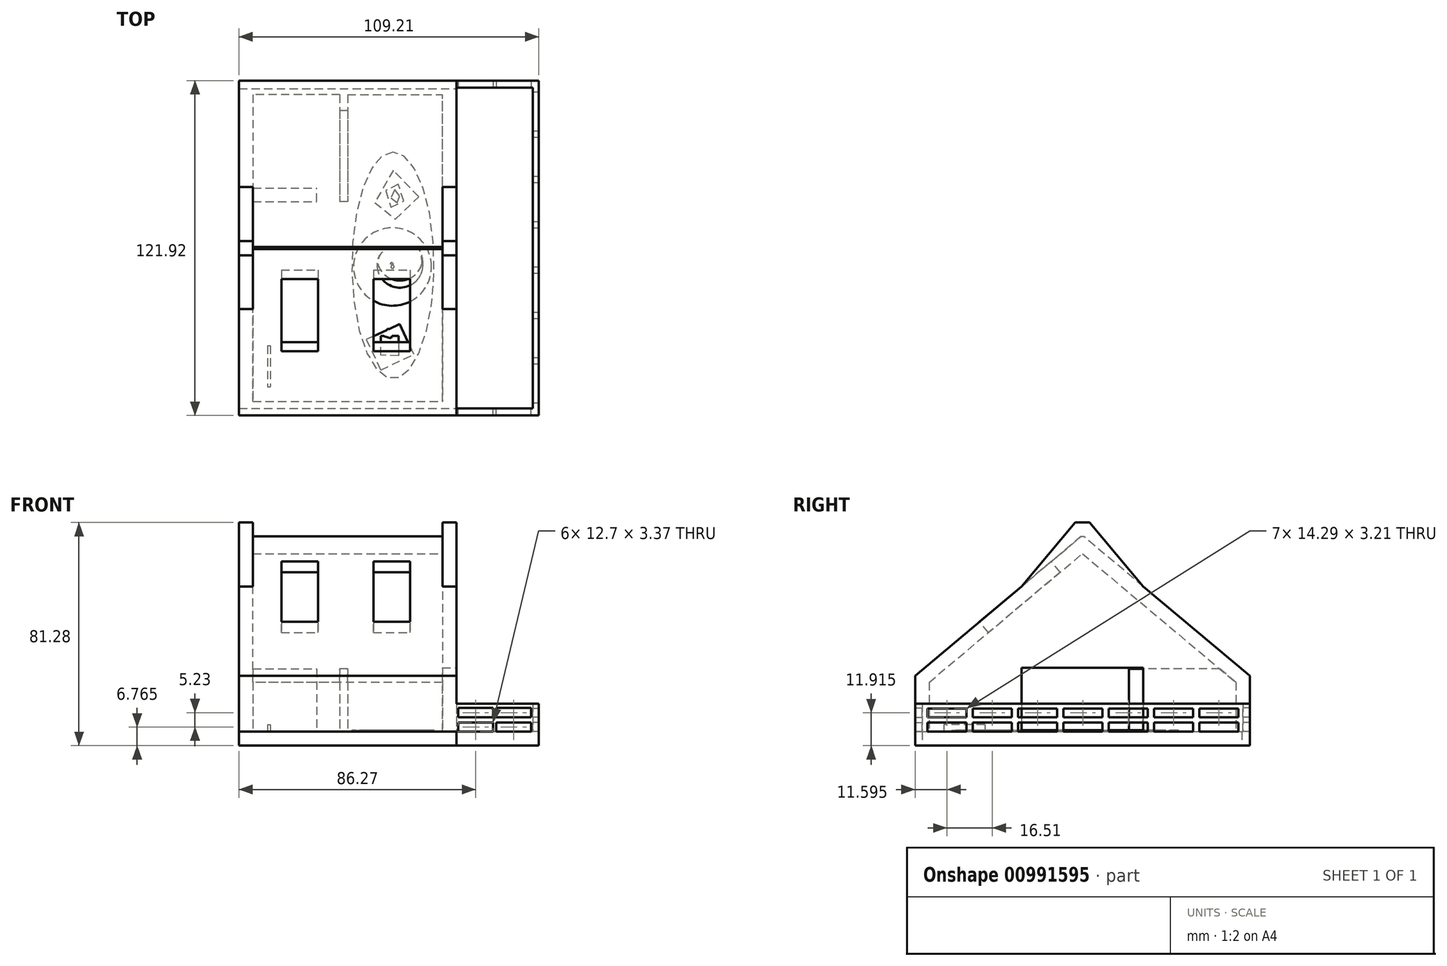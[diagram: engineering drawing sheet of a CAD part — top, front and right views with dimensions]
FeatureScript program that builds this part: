
annotation { "Feature Type Name" : "Feature", "Feature Type Description" : "" }
export const myFeature = defineFeature(function(context is Context, id is Id, definition is map)
    precondition{}
    {
        {
            var Q0;
            Q0=qCreatedBy(makeId("Top.planeOp"),FACE);
            var sketch = newSketch(context, id + "F0", { "sketchPlane" : qUnion([Q0])});
            skLineSegment(sketch, "E0.bottom", {"start": v(-69.71, 93.3) * mm, "end": v(39.5, 93.3) * mm});
            skLineSegment(sketch, "E0.top", {"start": v(-69.71, -28.62) * mm, "end": v(39.5, -28.62) * mm});
            skLineSegment(sketch, "E0.left", {"start": v(-69.71, 93.3) * mm, "end": v(-69.71, -28.62) * mm});
            skLineSegment(sketch, "E0.right", {"start": v(39.5, 93.3) * mm, "end": v(39.5, -28.62) * mm});
            skSolve(sketch);
        }
        {
            var Q0;
            Q0=makeQuery(id+"F0.imprint","IMPRINT",FACE,{"disambiguationData":[TD([[makeQuery(id+"F0.imprint","IMPRINT",EDGE,{"derivedFrom":sQuery(id+"F0.wireOp",EDGE,"E0.bottom")}),-1.0]])]});
            extrude(context, id + "F1", {"entities" : qUnion([Q0]), "depth" : 76.2 * mm, "offsetDistance" : 25.4 * mm});
        }
        {
            var Q0;
            Q0=makeQuery(id+"F1.opExtrude","CAP_FACE",FACE,{"disambiguationData":[OSD([sQuery(id+"F0.wireOp",EDGE,"E0.bottom"),sQuery(id+"F0.wireOp",EDGE,"E0.top"),sQuery(id+"F0.wireOp",EDGE,"E0.left"),sQuery(id+"F0.wireOp",EDGE,"E0.right")])],"isStart":false});
            var sketch = newSketch(context, id + "F2", { "sketchPlane" : qUnion([Q0])});
            skLineSegment(sketch, "E1.right", {"start": v(9.5, -28.62) * mm, "end": v(9.5, 93.3) * mm});
            skLineSegment(sketch, "E2.bottom", {"start": v(9.5, -28.62) * mm, "end": v(39.5, -28.62) * mm});
            skLineSegment(sketch, "E2.top", {"start": v(9.5, 93.3) * mm, "end": v(39.5, 93.3) * mm});
            skLineSegment(sketch, "E2.right", {"start": v(39.5, -28.62) * mm, "end": v(39.5, 93.3) * mm});
            skSolve(sketch);
        }
        {
            var Q0;
            Q0 = qSketchRegion(id + "F2", true);
            extrude(context, id + "F3", {"entities" : qUnion([Q0]), "operationType" : NewBodyOperationType.REMOVE, "oppositeDirection" : true, "depth" : 71.12 * mm, "offsetDistance" : 25.4 * mm});
        }
        {
            var Q0;
            Q0=makeQuery(id+"F1.opExtrude","CAP_EDGE",EDGE,{"disambiguationData":[OSD([sQuery(id+"F0.wireOp",EDGE,"E0.bottom")])],"isStart":false});
            var Q1;
            Q1=makeQuery(id+"F1.opExtrude","CAP_EDGE",EDGE,{"disambiguationData":[OSD([sQuery(id+"F0.wireOp",EDGE,"E0.top")])],"isStart":false});
            chamfer(context, id + "F4", {"entities" : qUnion([Q0, Q1]), "chamferType" : ChamferType.OFFSET_ANGLE, "width" : 50.8 * mm, "oppositeDirection" : false, "angle" : 50 * degree, "tangentPropagation" : true});
        }
        {
            var Q0;
            Q0=makeQuery(id+"F3.boolean.opBoolean","COPY",FACE,{"derivedFrom":makeQuery(id+"F3.opExtrude","SWEPT_FACE",FACE,{"disambiguationData":[OSD([sQuery(id+"F2.wireOp",EDGE,"E1.right")])]})});
            var Q1;
            Q1=makeQuery(id+"F1.opExtrude","SWEPT_FACE",FACE,{"disambiguationData":[OSD([sQuery(id+"F0.wireOp",EDGE,"E0.left")])]});
            shell(context, id + "F5", {"entities" : qUnion([Q0, Q1]), "thickness" : 5.08 * mm});
        }
        {
            var Q0;
            Q0=makeQuery(id+"F5.opShell","OFFSET_FACE",FACE,{"disambiguationData":[OSD([sQuery(id+"F0.wireOp",EDGE,"E0.bottom"),sQuery(id+"F0.wireOp",EDGE,"E0.top"),sQuery(id+"F0.wireOp",EDGE,"E0.left"),sQuery(id+"F0.wireOp",EDGE,"E0.right"),sQuery(id+"F2.wireOp",EDGE,"E2.bottom"),sQuery(id+"F2.wireOp",EDGE,"E2.top"),sQuery(id+"F2.wireOp",EDGE,"E1.right"),sQuery(id+"F2.wireOp",EDGE,"E2.right")])]});
            var sketch = newSketch(context, id + "F6", { "sketchPlane" : qUnion([Q0])});
            skPoint(sketch, "E3.oppositeSnap0", {"position": v(9.5, -26.08) * mm});
            skLineSegment(sketch, "E3.bottom", {"start": v(9.5, -28.62) * mm, "end": v(39.5, -28.62) * mm});
            skLineSegment(sketch, "E3.top", {"start": v(9.5, -26.08) * mm, "end": v(39.5, -26.08) * mm});
            skLineSegment(sketch, "E3.left", {"start": v(9.5, -28.62) * mm, "end": v(9.5, -26.08) * mm});
            skLineSegment(sketch, "E3.right", {"start": v(39.5, -28.62) * mm, "end": v(39.5, -26.08) * mm});
            skPoint(sketch, "E4.oppositeSnap0", {"position": v(9.5, 90.76) * mm});
            skLineSegment(sketch, "E4.bottom", {"start": v(9.5, 93.3) * mm, "end": v(39.5, 93.3) * mm});
            skLineSegment(sketch, "E4.top", {"start": v(9.5, 90.76) * mm, "end": v(39.5, 90.76) * mm});
            skLineSegment(sketch, "E4.left", {"start": v(9.5, 93.3) * mm, "end": v(9.5, 90.76) * mm});
            skLineSegment(sketch, "E4.right", {"start": v(39.5, 93.3) * mm, "end": v(39.5, 90.76) * mm});
            skLineSegment(sketch, "E5.bottom", {"start": v(39.5, -28.62) * mm, "end": v(37.37, -28.62) * mm});
            skLineSegment(sketch, "E5.top", {"start": v(39.5, 93.3) * mm, "end": v(37.37, 93.3) * mm});
            skLineSegment(sketch, "E5.left", {"start": v(39.5, -28.62) * mm, "end": v(39.5, 93.3) * mm});
            skLineSegment(sketch, "E5.right", {"start": v(37.37, -28.62) * mm, "end": v(37.37, 93.3) * mm});
            skLineSegment(sketch, "E6.bottom", {"start": v(9.5, -23.54) * mm, "end": v(4.43, -23.54) * mm});
            skLineSegment(sketch, "E6.top", {"start": v(9.5, 88.22) * mm, "end": v(4.43, 88.22) * mm});
            skLineSegment(sketch, "E6.left", {"start": v(9.5, -23.54) * mm, "end": v(9.5, 88.22) * mm});
            skLineSegment(sketch, "E6.right", {"start": v(4.43, -23.54) * mm, "end": v(4.43, 88.22) * mm});
            skLineSegment(sketch, "E7.bottom", {"start": v(-69.71, 88.22) * mm, "end": v(-64.63, 88.22) * mm});
            skLineSegment(sketch, "E7.top", {"start": v(-69.71, -23.54) * mm, "end": v(-64.63, -23.54) * mm});
            skLineSegment(sketch, "E7.left", {"start": v(-69.71, 88.22) * mm, "end": v(-69.71, -23.54) * mm});
            skLineSegment(sketch, "E7.right", {"start": v(-64.63, 88.22) * mm, "end": v(-64.63, -23.54) * mm});
            skLineSegment(sketch, "E8.bottom", {"start": v(-30.1, 88.22) * mm, "end": v(-32.97, 88.22) * mm});
            skLineSegment(sketch, "E8.top", {"start": v(-30.1, 49.23) * mm, "end": v(-32.97, 49.23) * mm});
            skLineSegment(sketch, "E8.left", {"start": v(-30.1, 88.22) * mm, "end": v(-30.1, 49.23) * mm});
            skLineSegment(sketch, "E8.right", {"start": v(-32.97, 88.22) * mm, "end": v(-32.97, 49.23) * mm});
            skLineSegment(sketch, "E9.bottom", {"start": v(-64.63, 49.23) * mm, "end": v(-41.45, 49.23) * mm});
            skLineSegment(sketch, "E9.top", {"start": v(-64.63, 54.2) * mm, "end": v(-41.45, 54.2) * mm});
            skLineSegment(sketch, "E9.left", {"start": v(-64.63, 49.23) * mm, "end": v(-64.63, 54.2) * mm});
            skLineSegment(sketch, "E9.right", {"start": v(-41.45, 49.23) * mm, "end": v(-41.45, 54.2) * mm});
            skEllipse(sketch, "E10", {"center": v(-13.6, 26.06) * mm, "majorRadius": 41.26 * mm, "minorRadius": 14.98 * mm, "majorAxis": v(0, 1)});
            skSolve(sketch);
        }
        {
            var Q0;
            Q0=makeQuery(id+"F6.imprint","IMPRINT",FACE,{"disambiguationData":[TD([[makeQuery(id+"F6.imprint","IMPRINT",EDGE,{"derivedFrom":sQuery(id+"F6.wireOp",EDGE,"E7.bottom")}),-1.0]])]});
            var Q1;
            Q1=makeQuery(id+"F6.imprint","IMPRINT",FACE,{"disambiguationData":[TD([[makeQuery(id+"F6.imprint","IMPRINT",EDGE,{"derivedFrom":sQuery(id+"F6.wireOp",EDGE,"E6.bottom")}),1.0]])]});
            var Q2;
            Q2 = qSketchRegion(id + "F9", true);
            extrude(context, id + "F7", {"entities" : qUnion([Q0, Q1, Q2]), "operationType" : NewBodyOperationType.ADD, "depth" : 76.2 * mm, "offsetDistance" : 25.4 * mm});
        }
        {
            var Q0;
            Q0=makeQuery(id+"F7.opExtrude","CAP_EDGE",EDGE,{"disambiguationData":[OSD([sQuery(id+"F6.wireOp",EDGE,"E6.top")])],"isStart":false});
            var Q1;
            Q1=makeQuery(id+"F7.opExtrude","CAP_EDGE",EDGE,{"disambiguationData":[OSD([sQuery(id+"F6.wireOp",EDGE,"E7.bottom")])],"isStart":false});
            var Q2;
            Q2=makeQuery(id+"F7.opExtrude","CAP_EDGE",EDGE,{"disambiguationData":[OSD([sQuery(id+"F6.wireOp",EDGE,"E6.bottom")])],"isStart":false});
            chamfer(context, id + "F8", {"entities" : qUnion([Q0, Q1, Q2]), "chamferType" : ChamferType.OFFSET_ANGLE, "width" : 63.5 * mm, "oppositeDirection" : false, "angle" : 40 * degree});
        }
        {
            var Q0;
            Q0=makeQuery(id+"F7.boolean.opBoolean","MERGE",FACE,{"derivedFrom":[makeQuery(id+"F1.opExtrude","SWEPT_FACE",FACE,{"disambiguationData":[OSD([sQuery(id+"F0.wireOp",EDGE,"E0.left")])]}),makeQuery(id+"F7.opExtrude","SWEPT_FACE",FACE,{"disambiguationData":[OSD([sQuery(id+"F6.wireOp",EDGE,"E7.left")])]})]});
            var sketch = newSketch(context, id + "F9", { "sketchPlane" : qUnion([Q0])});
            skLineSegment(sketch, "E11.0.0", {"start": v(-31.92, 76.2) * mm, "end": v(23.54, 29.66) * mm});
            skLineSegment(sketch, "E11.0.2", {"start": v(23.54, 29.66) * mm, "end": v(28.62, 25.4) * mm});
            skLineSegment(sketch, "E11.0.4", {"start": v(28.62, 25.4) * mm, "end": v(-10.15, 57.94) * mm});
            skLineSegment(sketch, "E11.0.6", {"start": v(-10.15, 57.94) * mm, "end": v(-31.92, 76.2) * mm});
            skLineSegment(sketch, "E12.0.0", {"start": v(-31.92, 76.2) * mm, "end": v(-10.15, 57.94) * mm});
            skLineSegment(sketch, "E12.0.1", {"start": v(-10.15, 57.94) * mm, "end": v(-29.74, 81.28) * mm});
            skLineSegment(sketch, "E12.0.2", {"start": v(-29.74, 81.28) * mm, "end": v(-34.94, 81.28) * mm});
            skLineSegment(sketch, "E12.0.3", {"start": v(-34.94, 81.28) * mm, "end": v(-54.52, 57.94) * mm});
            skLineSegment(sketch, "E12.0.4", {"start": v(-54.52, 57.94) * mm, "end": v(-32.76, 76.2) * mm});
            skLineSegment(sketch, "E12.0.5", {"start": v(-32.76, 76.2) * mm, "end": v(-31.92, 76.2) * mm});
            skLineSegment(sketch, "E13.0.1", {"start": v(-54.52, 57.94) * mm, "end": v(-93.3, 25.4) * mm});
            skLineSegment(sketch, "E13.0.2", {"start": v(-93.3, 25.4) * mm, "end": v(-93.3, 0) * mm});
            skLineSegment(sketch, "E13.0.3", {"start": v(-93.3, 0) * mm, "end": v(28.62, 0) * mm});
            skLineSegment(sketch, "E13.0.4", {"start": v(28.62, 0) * mm, "end": v(28.62, 25.4) * mm});
            skLineSegment(sketch, "E13.0.5", {"start": v(28.62, 25.4) * mm, "end": v(23.54, 29.66) * mm});
            skLineSegment(sketch, "E13.0.6", {"start": v(23.54, 29.66) * mm, "end": v(23.54, 81.28) * mm});
            skLineSegment(sketch, "E13.0.7", {"start": v(23.54, 81.28) * mm, "end": v(-34.94, 81.28) * mm});
            skSolve(sketch);
        }
        {
            var Q0;
            Q0=makeQuery(id+"F9.imprint","IMPRINT",FACE,{"disambiguationData":[TD([[makeQuery(id+"F9.imprint","IMPRINT",EDGE,{"derivedFrom":sQuery(id+"F9.wireOp",EDGE,"E11.0.4")}),-1.0]])]});
            extrude(context, id + "F10", {"entities" : qUnion([Q0]), "operationType" : NewBodyOperationType.REMOVE, "oppositeDirection" : true, "depth" : 25.4 * mm, "offsetDistance" : 25.4 * mm});
        }
        {
            var Q0;
            {var subQ0=sQuery(id+"F6.wireOp",EDGE,"E3.bottom");Q0=makeQuery(id+"F6.imprint","IMPRINT",FACE,{"disambiguationData":[TD([[makeQuery(id+"F6.imprint","IMPRINT",EDGE,{"derivedFrom":subQ0}),1.0]])]});}
            var Q1;
            {var subQ5=sQuery(id+"F6.wireOp",EDGE,"E5.bottom");Q1=makeQuery(id+"F6.imprint","IMPRINT",FACE,{"disambiguationData":[TD([[makeQuery(id+"F6.imprint","IMPRINT",EDGE,{"derivedFrom":subQ5}),1.0]])]});}
            var Q2;
            {var subQ0=sQuery(id+"F6.wireOp",EDGE,"E5.left");var subQ1=sQuery(id+"F6.wireOp",EDGE,"E3.top");var subQ2=makeQuery(id+"F6.imprint","INTERSECT",VERTEX,{"derivedFrom":[subQ1,subQ0]});Q2=makeQuery(id+"F6.imprint","IMPRINT",FACE,{"disambiguationData":[TD([[makeQuery(id+"F6.imprint","IMPRINT",EDGE,{"disambiguationData":[TD([[subQ2,1.0]])],"derivedFrom":subQ1}),1.0]])]});}
            var Q3;
            {var subQ0=sQuery(id+"F6.wireOp",EDGE,"E4.bottom");Q3=makeQuery(id+"F6.imprint","IMPRINT",FACE,{"disambiguationData":[TD([[makeQuery(id+"F6.imprint","IMPRINT",EDGE,{"derivedFrom":subQ0}),-1.0]])]});}
            var Q4;
            {var subQ5=sQuery(id+"F6.wireOp",EDGE,"E5.top");Q4=makeQuery(id+"F6.imprint","IMPRINT",FACE,{"disambiguationData":[TD([[makeQuery(id+"F6.imprint","IMPRINT",EDGE,{"derivedFrom":subQ5}),-1.0]])]});}
            extrude(context, id + "F11", {"entities" : qUnion([Q0, Q1, Q2, Q3, Q4]), "operationType" : NewBodyOperationType.ADD, "depth" : 10.16 * mm, "offsetDistance" : 25.4 * mm});
        }
        {
            var Q0;
            Q0=makeQuery(id+"F11.opExtrude","SWEPT_FACE",FACE,{"disambiguationData":[OSD([sQuery(id+"F6.wireOp",EDGE,"E5.right")])]});
            var sketch = newSketch(context, id + "F12", { "sketchPlane" : qUnion([Q0])});
            skLineSegment(sketch, "E14.bottom", {"start": v(-89.18, 5.08) * mm, "end": v(-74.89, 5.08) * mm});
            skLineSegment(sketch, "E14.top", {"start": v(-89.18, 8.45) * mm, "end": v(-74.89, 8.45) * mm});
            skLineSegment(sketch, "E14.left", {"start": v(-89.18, 5.08) * mm, "end": v(-89.18, 8.45) * mm});
            skLineSegment(sketch, "E14.right", {"start": v(-74.89, 5.08) * mm, "end": v(-74.89, 8.45) * mm});
            skLineSegment(sketch, "E15.bottom", {"start": v(-89.18, 10.31) * mm, "end": v(-74.89, 10.31) * mm});
            skLineSegment(sketch, "E15.top", {"start": v(-89.18, 13.52) * mm, "end": v(-74.89, 13.52) * mm});
            skLineSegment(sketch, "E15.left", {"start": v(-89.18, 10.31) * mm, "end": v(-89.18, 13.52) * mm});
            skLineSegment(sketch, "E15.right", {"start": v(-74.89, 10.31) * mm, "end": v(-74.89, 13.52) * mm});
            skLineSegment(sketch, "E16.1.0.0", {"start": v(-58.38, 5.08) * mm, "end": v(-58.38, 8.45) * mm});
            skLineSegment(sketch, "E16.1.0.1", {"start": v(-72.67, 5.08) * mm, "end": v(-58.38, 5.08) * mm});
            skLineSegment(sketch, "E16.1.0.2", {"start": v(-72.67, 10.31) * mm, "end": v(-72.67, 13.52) * mm});
            skLineSegment(sketch, "E16.1.0.3", {"start": v(-72.67, 10.31) * mm, "end": v(-58.38, 10.31) * mm});
            skLineSegment(sketch, "E16.1.0.4", {"start": v(-58.38, 10.31) * mm, "end": v(-58.38, 13.52) * mm});
            skLineSegment(sketch, "E16.1.0.5", {"start": v(-72.67, 8.45) * mm, "end": v(-58.38, 8.45) * mm});
            skLineSegment(sketch, "E16.1.0.6", {"start": v(-72.67, 13.52) * mm, "end": v(-58.38, 13.52) * mm});
            skLineSegment(sketch, "E16.1.0.7", {"start": v(-72.67, 5.08) * mm, "end": v(-72.67, 8.45) * mm});
            skLineSegment(sketch, "E16.2.0.0", {"start": v(-41.87, 5.08) * mm, "end": v(-41.87, 8.45) * mm});
            skLineSegment(sketch, "E16.2.0.1", {"start": v(-56.16, 5.08) * mm, "end": v(-41.87, 5.08) * mm});
            skLineSegment(sketch, "E16.2.0.2", {"start": v(-56.16, 10.31) * mm, "end": v(-56.16, 13.52) * mm});
            skLineSegment(sketch, "E16.2.0.3", {"start": v(-56.16, 10.31) * mm, "end": v(-41.87, 10.31) * mm});
            skLineSegment(sketch, "E16.2.0.4", {"start": v(-41.87, 10.31) * mm, "end": v(-41.87, 13.52) * mm});
            skLineSegment(sketch, "E16.2.0.5", {"start": v(-56.16, 8.45) * mm, "end": v(-41.87, 8.45) * mm});
            skLineSegment(sketch, "E16.2.0.6", {"start": v(-56.16, 13.52) * mm, "end": v(-41.87, 13.52) * mm});
            skLineSegment(sketch, "E16.2.0.7", {"start": v(-56.16, 5.08) * mm, "end": v(-56.16, 8.45) * mm});
            skLineSegment(sketch, "E16.3.0.0", {"start": v(-25.36, 5.08) * mm, "end": v(-25.36, 8.45) * mm});
            skLineSegment(sketch, "E16.3.0.1", {"start": v(-39.65, 5.08) * mm, "end": v(-25.36, 5.08) * mm});
            skLineSegment(sketch, "E16.3.0.2", {"start": v(-39.65, 10.31) * mm, "end": v(-39.65, 13.52) * mm});
            skLineSegment(sketch, "E16.3.0.3", {"start": v(-39.65, 10.31) * mm, "end": v(-25.36, 10.31) * mm});
            skLineSegment(sketch, "E16.3.0.4", {"start": v(-25.36, 10.31) * mm, "end": v(-25.36, 13.52) * mm});
            skLineSegment(sketch, "E16.3.0.5", {"start": v(-39.65, 8.45) * mm, "end": v(-25.36, 8.45) * mm});
            skLineSegment(sketch, "E16.3.0.6", {"start": v(-39.65, 13.52) * mm, "end": v(-25.36, 13.52) * mm});
            skLineSegment(sketch, "E16.3.0.7", {"start": v(-39.65, 5.08) * mm, "end": v(-39.65, 8.45) * mm});
            skLineSegment(sketch, "E16.4.0.0", {"start": v(-8.85, 5.08) * mm, "end": v(-8.85, 8.45) * mm});
            skLineSegment(sketch, "E16.4.0.1", {"start": v(-23.14, 5.08) * mm, "end": v(-8.85, 5.08) * mm});
            skLineSegment(sketch, "E16.4.0.2", {"start": v(-23.14, 10.31) * mm, "end": v(-23.14, 13.52) * mm});
            skLineSegment(sketch, "E16.4.0.3", {"start": v(-23.14, 10.31) * mm, "end": v(-8.85, 10.31) * mm});
            skLineSegment(sketch, "E16.4.0.4", {"start": v(-8.85, 10.31) * mm, "end": v(-8.85, 13.52) * mm});
            skLineSegment(sketch, "E16.4.0.5", {"start": v(-23.14, 8.45) * mm, "end": v(-8.85, 8.45) * mm});
            skLineSegment(sketch, "E16.4.0.6", {"start": v(-23.14, 13.52) * mm, "end": v(-8.85, 13.52) * mm});
            skLineSegment(sketch, "E16.4.0.7", {"start": v(-23.14, 5.08) * mm, "end": v(-23.14, 8.45) * mm});
            skLineSegment(sketch, "E16.5.0.0", {"start": v(7.66, 5.08) * mm, "end": v(7.66, 8.45) * mm});
            skLineSegment(sketch, "E16.5.0.1", {"start": v(-6.63, 5.08) * mm, "end": v(7.66, 5.08) * mm});
            skLineSegment(sketch, "E16.5.0.2", {"start": v(-6.63, 10.31) * mm, "end": v(-6.63, 13.52) * mm});
            skLineSegment(sketch, "E16.5.0.3", {"start": v(-6.63, 10.31) * mm, "end": v(7.66, 10.31) * mm});
            skLineSegment(sketch, "E16.5.0.4", {"start": v(7.66, 10.31) * mm, "end": v(7.66, 13.52) * mm});
            skLineSegment(sketch, "E16.5.0.5", {"start": v(-6.63, 8.45) * mm, "end": v(7.66, 8.45) * mm});
            skLineSegment(sketch, "E16.5.0.6", {"start": v(-6.63, 13.52) * mm, "end": v(7.66, 13.52) * mm});
            skLineSegment(sketch, "E16.5.0.7", {"start": v(-6.63, 5.08) * mm, "end": v(-6.63, 8.45) * mm});
            skLineSegment(sketch, "E16.6.0.0", {"start": v(24.17, 5.08) * mm, "end": v(24.17, 8.45) * mm});
            skLineSegment(sketch, "E16.6.0.1", {"start": v(9.88, 5.08) * mm, "end": v(24.17, 5.08) * mm});
            skLineSegment(sketch, "E16.6.0.2", {"start": v(9.88, 10.31) * mm, "end": v(9.88, 13.52) * mm});
            skLineSegment(sketch, "E16.6.0.3", {"start": v(9.88, 10.31) * mm, "end": v(24.17, 10.31) * mm});
            skLineSegment(sketch, "E16.6.0.4", {"start": v(24.17, 10.31) * mm, "end": v(24.17, 13.52) * mm});
            skLineSegment(sketch, "E16.6.0.5", {"start": v(9.88, 8.45) * mm, "end": v(24.17, 8.45) * mm});
            skLineSegment(sketch, "E16.6.0.6", {"start": v(9.88, 13.52) * mm, "end": v(24.17, 13.52) * mm});
            skLineSegment(sketch, "E16.6.0.7", {"start": v(9.88, 5.08) * mm, "end": v(9.88, 8.45) * mm});
            skLineSegment(sketch, "E16.direction1", {"start": v(-89.18, 5.08) * mm, "end": v(-72.67, 5.08) * mm, "construction": true});
            skSolve(sketch);
        }
        {
            var Q0;
            Q0 = qSketchRegion(id + "F12", true);
            extrude(context, id + "F13", {"entities" : qUnion([Q0]), "operationType" : NewBodyOperationType.REMOVE, "oppositeDirection" : true, "depth" : 5.08 * mm, "offsetDistance" : 25.4 * mm});
        }
        {
            var Q0;
            Q0=makeQuery(id+"F11.opExtrude","SWEPT_FACE",FACE,{"disambiguationData":[OSD([sQuery(id+"F6.wireOp",EDGE,"E3.top")])]});
            var sketch = newSketch(context, id + "F14", { "sketchPlane" : qUnion([Q0])});
            skLineSegment(sketch, "E17.bottom", {"start": v(-36.75, 5.08) * mm, "end": v(-24.05, 5.08) * mm});
            skLineSegment(sketch, "E17.top", {"start": v(-36.75, 8.45) * mm, "end": v(-24.05, 8.45) * mm});
            skLineSegment(sketch, "E17.left", {"start": v(-36.75, 5.08) * mm, "end": v(-36.75, 8.45) * mm});
            skLineSegment(sketch, "E17.right", {"start": v(-24.05, 5.08) * mm, "end": v(-24.05, 8.45) * mm});
            skLineSegment(sketch, "E18.0.1.0", {"start": v(-24.05, 10.31) * mm, "end": v(-24.05, 13.68) * mm});
            skLineSegment(sketch, "E18.0.1.1", {"start": v(-36.75, 13.68) * mm, "end": v(-24.05, 13.68) * mm});
            skLineSegment(sketch, "E18.0.1.2", {"start": v(-36.75, 10.31) * mm, "end": v(-24.05, 10.31) * mm});
            skLineSegment(sketch, "E18.0.1.3", {"start": v(-36.75, 10.31) * mm, "end": v(-36.75, 13.68) * mm});
            skLineSegment(sketch, "E18.1.0.0", {"start": v(-10.23, 5.08) * mm, "end": v(-10.23, 8.45) * mm});
            skLineSegment(sketch, "E18.1.0.1", {"start": v(-22.93, 8.45) * mm, "end": v(-10.23, 8.45) * mm});
            skLineSegment(sketch, "E18.1.0.2", {"start": v(-22.93, 5.08) * mm, "end": v(-10.23, 5.08) * mm});
            skLineSegment(sketch, "E18.1.0.3", {"start": v(-22.93, 5.08) * mm, "end": v(-22.93, 8.45) * mm});
            skLineSegment(sketch, "E18.1.1.0", {"start": v(-10.23, 10.31) * mm, "end": v(-10.23, 13.68) * mm});
            skLineSegment(sketch, "E18.1.1.1", {"start": v(-22.93, 13.68) * mm, "end": v(-10.23, 13.68) * mm});
            skLineSegment(sketch, "E18.1.1.2", {"start": v(-22.93, 10.31) * mm, "end": v(-10.23, 10.31) * mm});
            skLineSegment(sketch, "E18.1.1.3", {"start": v(-22.93, 10.31) * mm, "end": v(-22.93, 13.68) * mm});
            skLineSegment(sketch, "E18.direction1", {"start": v(-36.75, 5.08) * mm, "end": v(-22.93, 5.08) * mm, "construction": true});
            skLineSegment(sketch, "E18.direction2", {"start": v(-36.75, 5.08) * mm, "end": v(-36.75, 10.31) * mm, "construction": true});
            skSolve(sketch);
        }
        {
            var Q0;
            Q0 = qSketchRegion(id + "F14", true);
            extrude(context, id + "F15", {"entities" : qUnion([Q0]), "operationType" : NewBodyOperationType.REMOVE, "oppositeDirection" : true, "depth" : 5.08 * mm, "offsetDistance" : 25.4 * mm});
        }
        {
            var Q0;
            Q0=makeQuery(id+"F11.opExtrude","SWEPT_FACE",FACE,{"disambiguationData":[OSD([sQuery(id+"F6.wireOp",EDGE,"E4.top")])]});
            var sketch = newSketch(context, id + "F16", { "sketchPlane" : qUnion([Q0])});
            skLineSegment(sketch, "E19.bottom", {"start": v(10.21, 5.08) * mm, "end": v(22.91, 5.08) * mm});
            skLineSegment(sketch, "E19.top", {"start": v(10.21, 8.45) * mm, "end": v(22.91, 8.45) * mm});
            skLineSegment(sketch, "E19.left", {"start": v(10.21, 5.08) * mm, "end": v(10.21, 8.45) * mm});
            skLineSegment(sketch, "E19.right", {"start": v(22.91, 5.08) * mm, "end": v(22.91, 8.45) * mm});
            skLineSegment(sketch, "E20.0.1.0", {"start": v(22.91, 10.31) * mm, "end": v(22.91, 13.68) * mm});
            skLineSegment(sketch, "E20.0.1.1", {"start": v(10.21, 13.68) * mm, "end": v(22.91, 13.68) * mm});
            skLineSegment(sketch, "E20.0.1.2", {"start": v(10.21, 10.31) * mm, "end": v(22.91, 10.31) * mm});
            skLineSegment(sketch, "E20.0.1.3", {"start": v(10.21, 10.31) * mm, "end": v(10.21, 13.68) * mm});
            skLineSegment(sketch, "E20.1.0.0", {"start": v(36.73, 5.08) * mm, "end": v(36.73, 8.45) * mm});
            skLineSegment(sketch, "E20.1.0.1", {"start": v(24.03, 8.45) * mm, "end": v(36.73, 8.45) * mm});
            skLineSegment(sketch, "E20.1.0.2", {"start": v(24.03, 5.08) * mm, "end": v(36.73, 5.08) * mm});
            skLineSegment(sketch, "E20.1.0.3", {"start": v(24.03, 5.08) * mm, "end": v(24.03, 8.45) * mm});
            skLineSegment(sketch, "E20.1.1.0", {"start": v(36.73, 10.31) * mm, "end": v(36.73, 13.68) * mm});
            skLineSegment(sketch, "E20.1.1.1", {"start": v(24.03, 13.68) * mm, "end": v(36.73, 13.68) * mm});
            skLineSegment(sketch, "E20.1.1.2", {"start": v(24.03, 10.31) * mm, "end": v(36.73, 10.31) * mm});
            skLineSegment(sketch, "E20.1.1.3", {"start": v(24.03, 10.31) * mm, "end": v(24.03, 13.68) * mm});
            skLineSegment(sketch, "E20.direction1", {"start": v(10.21, 5.08) * mm, "end": v(24.03, 5.08) * mm, "construction": true});
            skLineSegment(sketch, "E20.direction2", {"start": v(10.21, 5.08) * mm, "end": v(10.21, 10.31) * mm, "construction": true});
            skSolve(sketch);
        }
        {
            var Q0;
            Q0 = qSketchRegion(id + "F16", true);
            extrude(context, id + "F17", {"entities" : qUnion([Q0]), "operationType" : NewBodyOperationType.REMOVE, "oppositeDirection" : true, "depth" : 5.08 * mm, "offsetDistance" : 25.4 * mm});
        }
        {
            var Q0;
            Q0=makeQuery(id+"F7.boolean.opBoolean","MERGE",FACE,{"derivedFrom":[makeQuery(id+"F3.boolean.opBoolean","COPY",FACE,{"derivedFrom":makeQuery(id+"F3.opExtrude","SWEPT_FACE",FACE,{"disambiguationData":[OSD([sQuery(id+"F2.wireOp",EDGE,"E1.right")])]})}),makeQuery(id+"F7.opExtrude","SWEPT_FACE",FACE,{"disambiguationData":[OSD([sQuery(id+"F6.wireOp",EDGE,"E6.left")])]})]});
            var sketch = newSketch(context, id + "F18", { "sketchPlane" : qUnion([Q0])});
            skLineSegment(sketch, "E21.bottom", {"start": v(10.15, 28.35) * mm, "end": v(54.52, 28.35) * mm});
            skLineSegment(sketch, "E21.top", {"start": v(10.15, 5.08) * mm, "end": v(54.52, 5.08) * mm});
            skLineSegment(sketch, "E21.left", {"start": v(10.15, 28.35) * mm, "end": v(10.15, 5.08) * mm});
            skLineSegment(sketch, "E21.right", {"start": v(54.52, 28.35) * mm, "end": v(54.52, 5.08) * mm});
            skSolve(sketch);
        }
        {
            var Q0;
            Q0=makeQuery(id+"F18.imprint","IMPRINT",FACE,{"disambiguationData":[TD([[makeQuery(id+"F18.imprint","IMPRINT",EDGE,{"derivedFrom":sQuery(id+"F18.wireOp",EDGE,"E21.bottom")}),-1.0]])]});
            extrude(context, id + "F19", {"entities" : qUnion([Q0]), "operationType" : NewBodyOperationType.REMOVE, "oppositeDirection" : true, "depth" : 5.08 * mm, "offsetDistance" : 25.4 * mm});
        }
        {
            var Q0;
            Q0=makeQuery(id+"F10.boolean.opBoolean","MERGE",FACE,{"derivedFrom":[makeQuery(id+"F4.opChamfer","BLEND_FACE",FACE,{"disambiguationData":[OSD([sQuery(id+"F0.wireOp",EDGE,"E0.top")])]})],"fromTools":[makeQuery(id+"F10.opExtrude","SWEPT_FACE",FACE,{"disambiguationData":[OSD([sQuery(id+"F9.wireOp",EDGE,"E11.0.4")])]})]});
            var sketch = newSketch(context, id + "F20", { "sketchPlane" : qUnion([Q0])});
            skPoint(sketch, "E22.firstSnap0", {"position": v(-64.63, 59.23) * mm});
            skLineSegment(sketch, "E22.bottom", {"start": v(-54.26, 59.23) * mm, "end": v(-40.94, 59.23) * mm});
            skLineSegment(sketch, "E22.top", {"start": v(-54.26, 25) * mm, "end": v(-40.94, 25) * mm});
            skLineSegment(sketch, "E22.left", {"start": v(-54.26, 59.23) * mm, "end": v(-54.26, 25) * mm});
            skLineSegment(sketch, "E22.right", {"start": v(-40.94, 59.23) * mm, "end": v(-40.94, 25) * mm});
            skLineSegment(sketch, "E23.1.0.0", {"start": v(-20.74, 25) * mm, "end": v(-7.41, 25) * mm});
            skLineSegment(sketch, "E23.1.0.1", {"start": v(-7.41, 59.23) * mm, "end": v(-7.41, 25) * mm});
            skLineSegment(sketch, "E23.1.0.2", {"start": v(-20.74, 59.23) * mm, "end": v(-20.74, 25) * mm});
            skLineSegment(sketch, "E23.1.0.3", {"start": v(-20.74, 59.23) * mm, "end": v(-7.41, 59.23) * mm});
            skLineSegment(sketch, "E23.direction1", {"start": v(-54.26, 25) * mm, "end": v(-20.74, 25) * mm, "construction": true});
            skSolve(sketch);
        }
        {
            var Q0;
            Q0 = qSketchRegion(id + "F20", true);
            extrude(context, id + "F21", {"entities" : qUnion([Q0]), "operationType" : NewBodyOperationType.REMOVE, "oppositeDirection" : true, "depth" : 5.08 * mm, "offsetDistance" : 25.4 * mm});
        }
        {
            var Q0;
            Q0=makeQuery(id+"F6.imprint","IMPRINT",FACE,{"disambiguationData":[TD([[makeQuery(id+"F6.imprint","IMPRINT",EDGE,{"derivedFrom":sQuery(id+"F6.wireOp",EDGE,"E9.bottom")}),1.0]])]});
            var Q1;
            Q1=makeQuery(id+"F6.imprint","IMPRINT",FACE,{"disambiguationData":[TD([[makeQuery(id+"F6.imprint","IMPRINT",EDGE,{"derivedFrom":sQuery(id+"F6.wireOp",EDGE,"E8.bottom")}),-1.0]])]});
            extrude(context, id + "F22", {"entities" : qUnion([Q0, Q1]), "operationType" : NewBodyOperationType.ADD, "depth" : 22.86 * mm, "offsetDistance" : 25.4 * mm});
        }
        {
            var Q0;
            Q0=makeQuery(id+"F6.imprint","IMPRINT",FACE,{"disambiguationData":[TD([[makeQuery(id+"F6.imprint","IMPRINT",EDGE,{"derivedFrom":sQuery(id+"F6.wireOp",EDGE,"E10")}),1.0]])]});
            extrude(context, id + "F23", {"entities" : qUnion([Q0]), "operationType" : NewBodyOperationType.ADD, "depth" : 0.25 * mm, "offsetDistance" : 25.4 * mm});
        }
        {
            var Q0;
            Q0=makeQuery(id+"F23.opExtrude","CAP_FACE",FACE,{"disambiguationData":[OSD([sQuery(id+"F6.wireOp",EDGE,"E10")])],"isStart":false});
            var sketch = newSketch(context, id + "F24", { "sketchPlane" : qUnion([Q0])});
            skArc(sketch, "E24", {"start": v(-13.6, 26.06) * mm, "mid": v(-13.87, 26.97) * mm, "end": v(-14.62, 26.38) * mm});
            skArc(sketch, "E25", {"start": v(-14.62, 26.38) * mm, "mid": v(-10.97, 22.3) * mm, "end": v(-7.32, 26.38) * mm});
            skArc(sketch, "E26", {"start": v(-7.32, 26.38) * mm, "mid": v(-13.2, 32.68) * mm, "end": v(-19.07, 26.38) * mm});
            skArc(sketch, "E27", {"start": v(-19.07, 26.38) * mm, "mid": v(-11.07, 20.51) * mm, "end": v(-3.1, 26.42) * mm});
            skArc(sketch, "E28", {"start": v(-3.1, 26.42) * mm, "mid": v(-13.68, 37.98) * mm, "end": v(-24.25, 26.42) * mm});
            skArc(sketch, "E29", {"start": v(-13.92, 26.06) * mm, "mid": v(-13.76, 24.94) * mm, "end": v(-13.6, 26.06) * mm});
            skArc(sketch, "E30", {"start": v(-13.92, 26.06) * mm, "mid": v(-14.36, 26.55) * mm, "end": v(-14.8, 26.06) * mm});
            skArc(sketch, "E31", {"start": v(-14.8, 26.06) * mm, "mid": v(-11.93, 22.8) * mm, "end": v(-8.47, 25.42) * mm});
            skArc(sketch, "E32", {"start": v(-8.47, 25.42) * mm, "mid": v(-13.7, 32.14) * mm, "end": v(-19.4, 25.8) * mm});
            skArc(sketch, "E33", {"start": v(-19.4, 25.8) * mm, "mid": v(-10.54, 17.92) * mm, "end": v(-2.66, 26.8) * mm});
            skArc(sketch, "E34", {"start": v(-2.66, 26.8) * mm, "mid": v(-13.64, 37.4) * mm, "end": v(-24.25, 26.42) * mm});
            skCircle(sketch, "E35", {"center": v(-13.76, 25.52) * mm, "radius": 14.2 * mm});
            skLineSegment(sketch, "E36", {"start": v(-23.35, -0.92) * mm, "end": v(-18.02, -12.09) * mm});
            skLineSegment(sketch, "E37", {"start": v(-18.02, -12.09) * mm, "end": v(-5.98, -6.35) * mm});
            skLineSegment(sketch, "E38", {"start": v(-5.98, -6.35) * mm, "end": v(-11.2, 4.6) * mm});
            skLineSegment(sketch, "E39", {"start": v(-11.2, 4.6) * mm, "end": v(-23.35, -0.92) * mm});
            skLineSegment(sketch, "E40", {"start": v(-18.07, -6.7) * mm, "end": v(-18.07, 0.38) * mm});
            skLineSegment(sketch, "E41", {"start": v(-18.07, 0.38) * mm, "end": v(-11.56, 0.38) * mm});
            skLineSegment(sketch, "E42", {"start": v(-11.56, 0.38) * mm, "end": v(-11.56, -6.92) * mm});
            skLineSegment(sketch, "E43", {"start": v(-11.56, -6.92) * mm, "end": v(-18.07, -6.7) * mm});
            skLineSegment(sketch, "E44", {"start": v(-16.93, 0.19) * mm, "end": v(-14.35, -0.53) * mm});
            skLineSegment(sketch, "E45", {"start": v(-14.35, -0.53) * mm, "end": v(-13.24, 1.97) * mm});
            skLineSegment(sketch, "E46", {"start": v(-13.24, 1.97) * mm, "end": v(-15.56, 3) * mm});
            skLineSegment(sketch, "E47", {"start": v(-15.56, 3) * mm, "end": v(-16.93, 0.19) * mm});
            skLineSegment(sketch, "E48", {"start": v(-20.23, 48.91) * mm, "end": v(-12.74, 42.9) * mm});
            skLineSegment(sketch, "E49", {"start": v(-12.74, 42.9) * mm, "end": v(-4.23, 50.98) * mm});
            skLineSegment(sketch, "E50", {"start": v(-4.23, 50.98) * mm, "end": v(-13.44, 60.67) * mm});
            skLineSegment(sketch, "E51", {"start": v(-13.44, 60.67) * mm, "end": v(-20.23, 48.91) * mm});
            skLineSegment(sketch, "E52", {"start": v(-16.2, 53.3) * mm, "end": v(-14.36, 47.22) * mm});
            skLineSegment(sketch, "E53", {"start": v(-14.36, 47.22) * mm, "end": v(-9.67, 49.46) * mm});
            skLineSegment(sketch, "E54", {"start": v(-9.67, 49.46) * mm, "end": v(-11.66, 55.6) * mm});
            skLineSegment(sketch, "E55", {"start": v(-11.66, 55.6) * mm, "end": v(-16.2, 53.3) * mm});
            skLineSegment(sketch, "E56", {"start": v(-14.36, 50.6) * mm, "end": v(-12.01, 48.91) * mm});
            skPoint(sketch, "E56.endSnap0", {"position": v(-12.01, 48.34) * mm});
            skLineSegment(sketch, "E57", {"start": v(-12.01, 48.91) * mm, "end": v(-11.19, 51.29) * mm});
            skLineSegment(sketch, "E58", {"start": v(-11.19, 51.29) * mm, "end": v(-12.99, 53.67) * mm});
            skLineSegment(sketch, "E59", {"start": v(-12.99, 53.67) * mm, "end": v(-14.36, 50.6) * mm});
            skSolve(sketch);
        }
        {
            var Q0;
            Q0=makeQuery(id+"F24.imprint","IMPRINT",FACE,{"disambiguationData":[TD([[makeQuery(id+"F24.imprint","IMPRINT",EDGE,{"derivedFrom":sQuery(id+"F24.wireOp",EDGE,"E24")}),1.0]])]});
            var Q1;
            Q1=makeQuery(id+"F24.imprint","IMPRINT",FACE,{"disambiguationData":[TD([[makeQuery(id+"F24.imprint","IMPRINT",EDGE,{"derivedFrom":sQuery(id+"F24.wireOp",EDGE,"E35")}),-1.0]])]});
            var Q2;
            Q2=makeQuery(id+"F24.imprint","IMPRINT",FACE,{"disambiguationData":[TD([[makeQuery(id+"F24.imprint","IMPRINT",EDGE,{"derivedFrom":sQuery(id+"F24.wireOp",EDGE,"E40")}),-1.0]])]});
            var Q3;
            Q3=makeQuery(id+"F24.imprint","IMPRINT",FACE,{"disambiguationData":[TD([[makeQuery(id+"F24.imprint","IMPRINT",EDGE,{"derivedFrom":sQuery(id+"F24.wireOp",EDGE,"E52")}),1.0]])]});
            var Q4;
            {var subQ1=sQuery(id+"F24.wireOp",EDGE,"E27");Q4=makeQuery(id+"F24.imprint","IMPRINT",FACE,{"disambiguationData":[TD([[makeQuery(id+"F24.imprint","IMPRINT",EDGE,{"derivedFrom":subQ1}),-1.0]])]});}
            extrude(context, id + "F25", {"entities" : qUnion([Q0, Q1, Q2, Q3, Q4]), "operationType" : NewBodyOperationType.ADD, "depth" : 0.25 * mm, "offsetDistance" : 25.4 * mm});
        }
        {
            var Q0;
            {var subQ4=sQuery(id+"F6.wireOp",EDGE,"E6.right");Q0=makeQuery(id+"F6.imprint","IMPRINT",FACE,{"disambiguationData":[TD([[makeQuery(id+"F6.imprint","IMPRINT",EDGE,{"derivedFrom":subQ4}),1.0]])]});}
            var sketch = newSketch(context, id + "F26", { "sketchPlane" : qUnion([Q0])});
            skLineSegment(sketch, "E60.bottom", {"start": v(-59.26, -3.22) * mm, "end": v(-58.23, -3.22) * mm});
            skLineSegment(sketch, "E60.top", {"start": v(-59.26, -18.15) * mm, "end": v(-58.23, -18.15) * mm});
            skLineSegment(sketch, "E60.left", {"start": v(-59.26, -3.22) * mm, "end": v(-59.26, -18.15) * mm});
            skLineSegment(sketch, "E60.right", {"start": v(-58.23, -3.22) * mm, "end": v(-58.23, -18.15) * mm});
            skSolve(sketch);
        }
        {
            var Q0;
            {var subQ0=sQuery(id+"F26.wireOp",EDGE,"E60.bottom");Q0=makeQuery(id+"F26.imprint","IMPRINT",FACE,{"disambiguationData":[TD([[makeQuery(id+"F26.imprint","IMPRINT",EDGE,{"derivedFrom":subQ0}),-1.0]])]});}
            extrude(context, id + "F27", {"entities" : qUnion([Q0]), "operationType" : NewBodyOperationType.ADD, "depth" : 2.54 * mm, "offsetDistance" : 25.4 * mm});
        }
        {
            var Q0;
            Q0=makeQuery(id+"F1.opExtrude","CAP_FACE",FACE,{"disambiguationData":[OSD([sQuery(id+"F0.wireOp",EDGE,"E0.bottom"),sQuery(id+"F0.wireOp",EDGE,"E0.top"),sQuery(id+"F0.wireOp",EDGE,"E0.left"),sQuery(id+"F0.wireOp",EDGE,"E0.right")])],"isStart":true});
            var sketch = newSketch(context, id + "F28", { "sketchPlane" : qUnion([Q0])});
            skLineSegment(sketch, "E61.bottom", {"start": v(-69.71, 28.62) * mm, "end": v(9.5, 28.62) * mm});
            skLineSegment(sketch, "E61.top", {"start": v(-69.71, 26.09) * mm, "end": v(9.5, 26.09) * mm});
            skLineSegment(sketch, "E61.left", {"start": v(-69.71, 28.62) * mm, "end": v(-69.71, 26.09) * mm});
            skLineSegment(sketch, "E61.right", {"start": v(9.5, 28.62) * mm, "end": v(9.5, 26.09) * mm});
            skLineSegment(sketch, "E62.bottom", {"start": v(-69.71, -93.3) * mm, "end": v(9.5, -93.3) * mm});
            skLineSegment(sketch, "E62.top", {"start": v(-69.71, -90.39) * mm, "end": v(9.5, -90.39) * mm});
            skLineSegment(sketch, "E62.left", {"start": v(-69.71, -93.3) * mm, "end": v(-69.71, -90.39) * mm});
            skLineSegment(sketch, "E62.right", {"start": v(9.5, -93.3) * mm, "end": v(9.5, -90.39) * mm});
            skSolve(sketch);
        }
        {
            var Q0;
            Q0=makeQuery(id+"F28.imprint","IMPRINT",FACE,{"disambiguationData":[TD([[makeQuery(id+"F28.imprint","IMPRINT",EDGE,{"derivedFrom":sQuery(id+"F28.wireOp",EDGE,"E61.bottom")}),-1.0]])]});
            var Q1;
            Q1=makeQuery(id+"F28.imprint","IMPRINT",FACE,{"disambiguationData":[TD([[makeQuery(id+"F28.imprint","IMPRINT",EDGE,{"derivedFrom":sQuery(id+"F28.wireOp",EDGE,"E62.bottom")}),1.0]])]});
            extrude(context, id + "F29", {"entities" : qUnion([Q0, Q1]), "operationType" : NewBodyOperationType.REMOVE, "oppositeDirection" : true, "depth" : 5.05 * mm, "offsetDistance" : 25.4 * mm});
        }
    });
